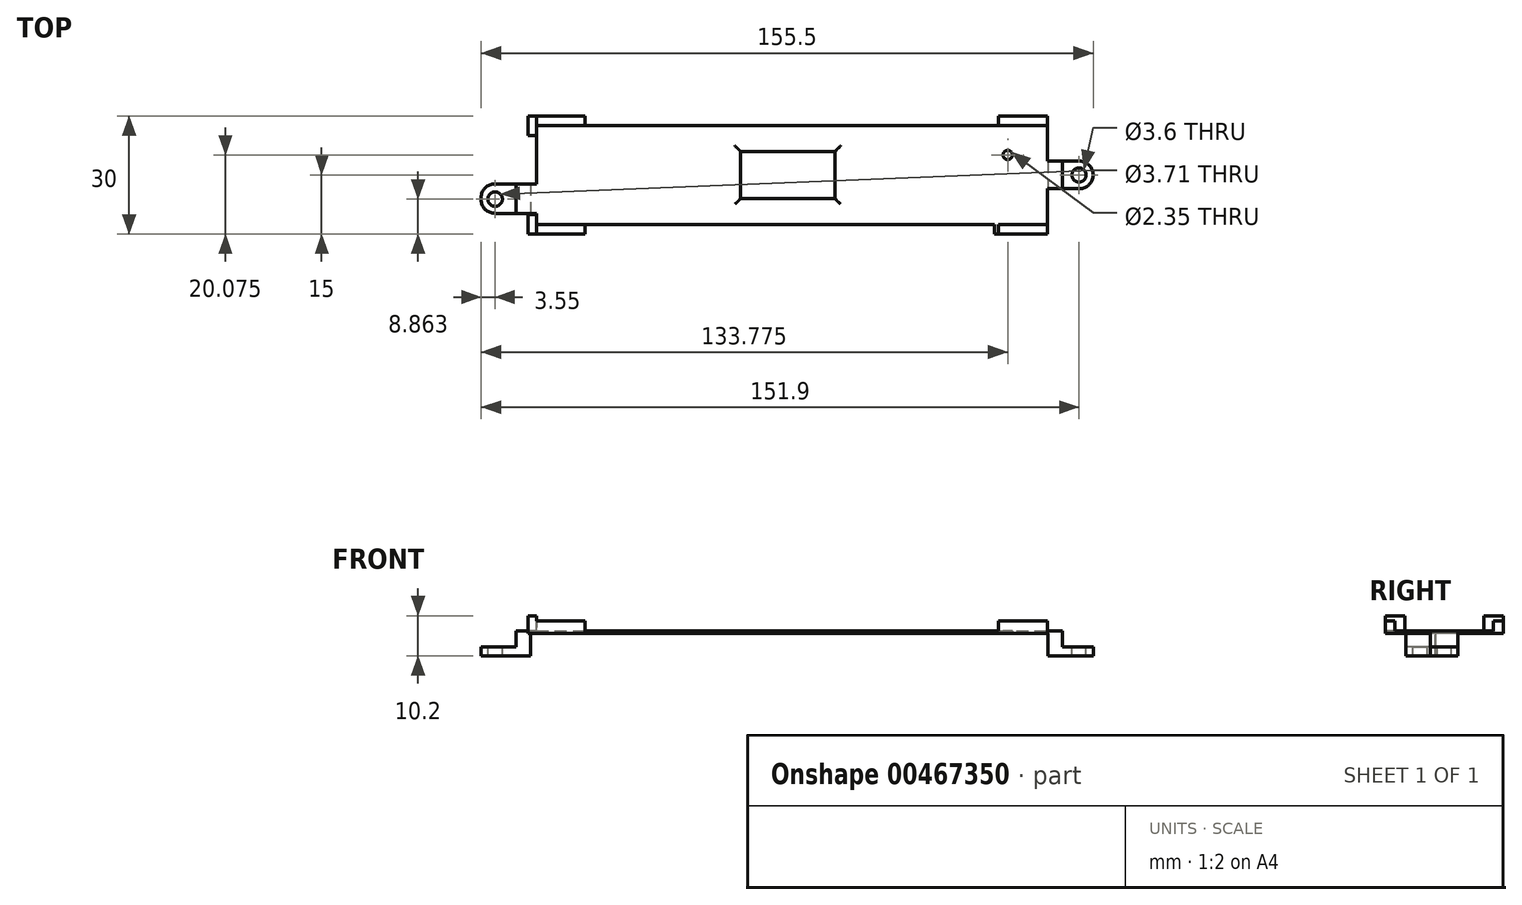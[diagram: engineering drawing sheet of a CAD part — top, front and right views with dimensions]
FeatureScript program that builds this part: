
annotation { "Feature Type Name" : "Feature", "Feature Type Description" : "" }
export const myFeature = defineFeature(function(context is Context, id is Id, definition is map)
    precondition{}
    {
        {
            var Q0;
            Q0=qCreatedBy(makeId("Top.planeOp"),FACE);
            var sketch = newSketch(context, id + "F0", { "sketchPlane" : qUnion([Q0])});
            skLineSegment(sketch, "E0.bottom", {"start": v(-66, 15) * mm, "end": v(-51.5, 15) * mm});
            skLineSegment(sketch, "E0.top", {"start": v(-66, -15) * mm, "end": v(-51.5, -15) * mm});
            skLineSegment(sketch, "E0.left", {"start": v(-66, 15) * mm, "end": v(-66, 10) * mm});
            skLineSegment(sketch, "E0.right", {"start": v(66, 15) * mm, "end": v(66, -15) * mm});
            skLineSegment(sketch, "E1.bottom", {"start": v(-51.5, 12.55) * mm, "end": v(53.5, 12.55) * mm});
            skLineSegment(sketch, "E1.top", {"start": v(-51.5, -12.55) * mm, "end": v(52.5, -12.55) * mm});
            skLineSegment(sketch, "E2", {"start": v(-51.5, 12.55) * mm, "end": v(-51.5, 15) * mm});
            skLineSegment(sketch, "E3", {"start": v(-51.5, -12.55) * mm, "end": v(-51.5, -15) * mm});
            skLineSegment(sketch, "E4", {"start": v(52.5, -12.55) * mm, "end": v(52.5, -15) * mm});
            skLineSegment(sketch, "E5", {"start": v(53.5, 12.55) * mm, "end": v(53.5, 15) * mm});
            skLineSegment(sketch, "E6.trimOffspring", {"start": v(52.5, -15) * mm, "end": v(66, -15) * mm});
            skLineSegment(sketch, "E7.trimOffspring", {"start": v(53.5, 15) * mm, "end": v(66, 15) * mm});
            skLineSegment(sketch, "E8.bottom", {"start": v(-12, 6) * mm, "end": v(12, 6) * mm});
            skLineSegment(sketch, "E8.top", {"start": v(-12, -6) * mm, "end": v(12, -6) * mm});
            skLineSegment(sketch, "E8.left", {"start": v(-12, 6) * mm, "end": v(-12, -6) * mm});
            skLineSegment(sketch, "E8.right", {"start": v(12, 6) * mm, "end": v(12, -6) * mm});
            skLineSegment(sketch, "E9.bottom", {"start": v(-66, 10) * mm, "end": v(-63.8, 10) * mm});
            skLineSegment(sketch, "E9.top", {"start": v(-66, -10) * mm, "end": v(-63.8, -10) * mm});
            skLineSegment(sketch, "E9.right", {"start": v(-63.8, 10) * mm, "end": v(-63.8, -10) * mm});
            skLineSegment(sketch, "E10.trimOffspring", {"start": v(-66, -10) * mm, "end": v(-66, -15) * mm});
            skSolve(sketch);
        }
        {
            var Q0;
            Q0 = qSketchRegion(id + "F0", true);
            extrude(context, id + "F1", {"entities" : qUnion([Q0]), "depth" : 4.5 * mm});
        }
        {
            var Q0;
            Q0=makeQuery(id+"F1.opExtrude","CAP_FACE",FACE,{"disambiguationData":[OSD([sQuery(id+"F0.wireOp",EDGE,"E0.bottom"),sQuery(id+"F0.wireOp",EDGE,"E0.top"),sQuery(id+"F0.wireOp",EDGE,"E0.left"),sQuery(id+"F0.wireOp",EDGE,"E0.right"),sQuery(id+"F0.wireOp",EDGE,"E1.bottom"),sQuery(id+"F0.wireOp",EDGE,"E1.top"),sQuery(id+"F0.wireOp",EDGE,"E2"),sQuery(id+"F0.wireOp",EDGE,"E3"),sQuery(id+"F0.wireOp",EDGE,"E4"),sQuery(id+"F0.wireOp",EDGE,"E5"),sQuery(id+"F0.wireOp",EDGE,"E6.trimOffspring"),sQuery(id+"F0.wireOp",EDGE,"E7.trimOffspring"),sQuery(id+"F0.wireOp",EDGE,"E8.bottom"),sQuery(id+"F0.wireOp",EDGE,"E8.top"),sQuery(id+"F0.wireOp",EDGE,"E8.left"),sQuery(id+"F0.wireOp",EDGE,"E8.right")])],"isStart":false});
            var sketch = newSketch(context, id + "F2", { "sketchPlane" : qUnion([Q0])});
            skLineSegment(sketch, "E11.bottom", {"start": v(-63.8, 17.54) * mm, "end": v(70.25, 17.54) * mm});
            skLineSegment(sketch, "E11.top", {"start": v(-63.8, -19.78) * mm, "end": v(70.25, -19.78) * mm});
            skLineSegment(sketch, "E11.left", {"start": v(-63.8, 17.54) * mm, "end": v(-63.8, -19.78) * mm});
            skLineSegment(sketch, "E11.right", {"start": v(70.25, 17.54) * mm, "end": v(70.25, -19.78) * mm});
            skSolve(sketch);
        }
        {
            var Q0;
            Q0 = qSketchRegion(id + "F2", true);
            extrude(context, id + "F3", {"entities" : qUnion([Q0]), "operationType" : NewBodyOperationType.REMOVE, "oppositeDirection" : true, "depth" : 1.3 * mm});
        }
        {
            var Q0;
            Q0=makeQuery(id+"F3.boolean.opBoolean","COPY",FACE,{"derivedFrom":makeQuery(id+"F3.opExtrude","CAP_FACE",FACE,{"disambiguationData":[OSD([sQuery(id+"F2.wireOp",EDGE,"E11.bottom"),sQuery(id+"F2.wireOp",EDGE,"E11.top"),sQuery(id+"F2.wireOp",EDGE,"E11.left"),sQuery(id+"F2.wireOp",EDGE,"E11.right")])],"isStart":false})});
            var sketch = newSketch(context, id + "F4", { "sketchPlane" : qUnion([Q0])});
            skLineSegment(sketch, "E12.top", {"start": v(-63.8, -12.55) * mm, "end": v(-51.5, -12.55) * mm});
            skLineSegment(sketch, "E12.left", {"start": v(-63.8, 12.5) * mm, "end": v(-63.8, -12.55) * mm});
            skLineSegment(sketch, "E12.right", {"start": v(68.76, 12.5) * mm, "end": v(68.76, -12.55) * mm});
            skLineSegment(sketch, "E13.top", {"start": v(-51.5, 21.08) * mm, "end": v(53.5, 21.08) * mm});
            skLineSegment(sketch, "E13.left", {"start": v(-51.5, 12.55) * mm, "end": v(-51.5, 21.08) * mm});
            skLineSegment(sketch, "E13.right", {"start": v(53.5, 12.55) * mm, "end": v(53.5, 21.08) * mm});
            skLineSegment(sketch, "E14.top", {"start": v(-51.5, -30.05) * mm, "end": v(53.5, -30.05) * mm});
            skLineSegment(sketch, "E14.left", {"start": v(-51.5, -12.55) * mm, "end": v(-51.5, -30.05) * mm});
            skLineSegment(sketch, "E14.right", {"start": v(53.5, -12.55) * mm, "end": v(53.5, -30.05) * mm});
            skLineSegment(sketch, "E15.trimOffspring", {"start": v(53.5, -12.55) * mm, "end": v(68.76, -12.55) * mm});
            skLineSegment(sketch, "E16", {"start": v(-51.5, 12.55) * mm, "end": v(-63.8, 12.5) * mm});
            skLineSegment(sketch, "E17", {"start": v(68.76, 12.5) * mm, "end": v(53.5, 12.55) * mm});
            skSolve(sketch);
        }
        {
            var Q0;
            Q0 = qSketchRegion(id + "F4", true);
            extrude(context, id + "F5", {"entities" : qUnion([Q0]), "operationType" : NewBodyOperationType.REMOVE, "oppositeDirection" : true, "depth" : 2.6 * mm});
        }
        {
            var Q0;
            Q0=makeQuery(id+"F5.boolean.opBoolean","COPY",FACE,{"derivedFrom":makeQuery(id+"F5.opExtrude","CAP_FACE",FACE,{"disambiguationData":[OSD([sQuery(id+"F4.wireOp",EDGE,"E12.bottom"),sQuery(id+"F4.wireOp",EDGE,"E12.top"),sQuery(id+"F4.wireOp",EDGE,"E12.left"),sQuery(id+"F4.wireOp",EDGE,"E12.right")])],"isStart":false})});
            var sketch = newSketch(context, id + "F6", { "sketchPlane" : qUnion([Q0])});
            skLineSegment(sketch, "E18.bottom", {"start": v(66, -3.5) * mm, "end": v(74.1, -3.5) * mm});
            skLineSegment(sketch, "E18.top", {"start": v(66, 3.5) * mm, "end": v(74.1, 3.5) * mm});
            skLineSegment(sketch, "E18.left", {"start": v(66, -3.5) * mm, "end": v(66, 3.5) * mm});
            skLineSegment(sketch, "E18.right", {"start": v(77.6, 0) * mm, "end": v(77.6, 0) * mm});
            skCircle(sketch, "E19", {"center": v(74, 0) * mm, "radius": 1.8 * mm});
            skPoint(sketch, "E20.visualSharp", {"position": v(77.6, -3.5) * mm});
            skArc(sketch, "E20.filletArc", {"start": v(74.1, -3.5) * mm, "mid": v(76.57, -2.47) * mm, "end": v(77.6, 0) * mm});
            skPoint(sketch, "E21.visualSharp", {"position": v(77.6, 3.5) * mm});
            skArc(sketch, "E21.filletArc", {"start": v(77.6, 0) * mm, "mid": v(76.57, 2.47) * mm, "end": v(74.1, 3.5) * mm});
            skLineSegment(sketch, "E22.bottom", {"start": v(-63.8, -9.75) * mm, "end": v(-74.4, -9.75) * mm});
            skLineSegment(sketch, "E22.top", {"start": v(-63.8, -2.25) * mm, "end": v(-74.4, -2.25) * mm});
            skLineSegment(sketch, "E22.left", {"start": v(-63.8, -9.75) * mm, "end": v(-63.8, -2.25) * mm});
            skLineSegment(sketch, "E22.right", {"start": v(-77.9, -6.25) * mm, "end": v(-77.9, -5.75) * mm});
            skCircle(sketch, "E23", {"center": v(-74.35, -6.14) * mm, "radius": 1.85 * mm});
            skPoint(sketch, "E24.visualSharp", {"position": v(-77.9, -9.75) * mm});
            skArc(sketch, "E24.filletArc", {"start": v(-77.9, -6.25) * mm, "mid": v(-76.87, -8.72) * mm, "end": v(-74.4, -9.75) * mm});
            skPoint(sketch, "E25.visualSharp", {"position": v(-77.9, -2.25) * mm});
            skArc(sketch, "E25.filletArc", {"start": v(-74.4, -2.25) * mm, "mid": v(-76.87, -3.28) * mm, "end": v(-77.9, -5.75) * mm});
            skSolve(sketch);
        }
        {
            var Q0;
            Q0 = qSketchRegion(id + "F6", true);
            extrude(context, id + "F7", {"entities" : qUnion([Q0]), "operationType" : NewBodyOperationType.ADD, "oppositeDirection" : true, "depth" : 6.3 * mm});
        }
        {
            var Q0;
            Q0=makeQuery(id+"F7.opExtrude","CAP_FACE",FACE,{"disambiguationData":[OSD([sQuery(id+"F6.wireOp",EDGE,"E22.bottom"),sQuery(id+"F6.wireOp",EDGE,"E22.top"),sQuery(id+"F6.wireOp",EDGE,"E22.left"),sQuery(id+"F6.wireOp",EDGE,"E23"),sQuery(id+"F6.wireOp",EDGE,"E24.filletArc"),sQuery(id+"F6.wireOp",EDGE,"E25.filletArc")])],"isStart":false});
            var sketch = newSketch(context, id + "F8", { "sketchPlane" : qUnion([Q0])});
            skLineSegment(sketch, "E26.bottom", {"start": v(66.1, -31.39) * mm, "end": v(-65.37, -31.39) * mm});
            skLineSegment(sketch, "E26.top", {"start": v(66.1, 26.27) * mm, "end": v(-65.37, 26.27) * mm});
            skLineSegment(sketch, "E26.left", {"start": v(66.1, -31.39) * mm, "end": v(66.1, 26.27) * mm});
            skLineSegment(sketch, "E26.right", {"start": v(-65.37, -31.39) * mm, "end": v(-65.37, 26.27) * mm});
            skSolve(sketch);
        }
        {
            var Q0;
            Q0 = qSketchRegion(id + "F8", true);
            var Q1;
            Q1=makeQuery(id+"F1.opExtrude","CAP_FACE",FACE,{"disambiguationData":[OSD([sQuery(id+"F0.wireOp",EDGE,"E0.bottom"),sQuery(id+"F0.wireOp",EDGE,"E0.top"),sQuery(id+"F0.wireOp",EDGE,"E0.left"),sQuery(id+"F0.wireOp",EDGE,"E0.right"),sQuery(id+"F0.wireOp",EDGE,"E1.bottom"),sQuery(id+"F0.wireOp",EDGE,"E1.top"),sQuery(id+"F0.wireOp",EDGE,"E2"),sQuery(id+"F0.wireOp",EDGE,"E3"),sQuery(id+"F0.wireOp",EDGE,"E4"),sQuery(id+"F0.wireOp",EDGE,"E5"),sQuery(id+"F0.wireOp",EDGE,"E6.trimOffspring"),sQuery(id+"F0.wireOp",EDGE,"E7.trimOffspring"),sQuery(id+"F0.wireOp",EDGE,"E8.bottom"),sQuery(id+"F0.wireOp",EDGE,"E8.top"),sQuery(id+"F0.wireOp",EDGE,"E8.left"),sQuery(id+"F0.wireOp",EDGE,"E8.right"),sQuery(id+"F0.wireOp",EDGE,"E9.bottom"),sQuery(id+"F0.wireOp",EDGE,"E9.top"),sQuery(id+"F0.wireOp",EDGE,"E9.right"),sQuery(id+"F0.wireOp",EDGE,"E10.trimOffspring")])],"isStart":true});
            extrude(context, id + "F9", {"entities" : qUnion([Q0]), "operationType" : NewBodyOperationType.REMOVE, "endBound" : BoundingType.UP_TO_SURFACE, "oppositeDirection" : true, "endBoundEntityFace" : qUnion([Q1]), "depth" : 25 * mm});
        }
        {
            var Q0;
            {var subQ0=sQuery(id+"F0.wireOp",EDGE,"E10.trimOffspring");var subQ1=sQuery(id+"F0.wireOp",EDGE,"E9.right");var subQ2=sQuery(id+"F0.wireOp",EDGE,"E9.top");var subQ3=sQuery(id+"F0.wireOp",EDGE,"E9.bottom");var subQ4=sQuery(id+"F0.wireOp",EDGE,"E8.right");var subQ5=sQuery(id+"F0.wireOp",EDGE,"E8.left");var subQ6=sQuery(id+"F0.wireOp",EDGE,"E8.top");var subQ7=sQuery(id+"F0.wireOp",EDGE,"E8.bottom");var subQ8=sQuery(id+"F0.wireOp",EDGE,"E7.trimOffspring");var subQ9=sQuery(id+"F0.wireOp",EDGE,"E6.trimOffspring");var subQ10=sQuery(id+"F0.wireOp",EDGE,"E5");var subQ11=sQuery(id+"F0.wireOp",EDGE,"E4");var subQ12=sQuery(id+"F0.wireOp",EDGE,"E3");var subQ13=sQuery(id+"F0.wireOp",EDGE,"E2");var subQ14=sQuery(id+"F0.wireOp",EDGE,"E1.top");var subQ15=sQuery(id+"F0.wireOp",EDGE,"E1.bottom");var subQ16=sQuery(id+"F0.wireOp",EDGE,"E0.right");var subQ17=sQuery(id+"F0.wireOp",EDGE,"E0.left");var subQ18=sQuery(id+"F0.wireOp",EDGE,"E0.top");var subQ19=sQuery(id+"F0.wireOp",EDGE,"E0.bottom");Q0=makeQuery(id+"F9.boolean.opBoolean","MERGE",FACE,{"derivedFrom":[makeQuery(id+"F1.opExtrude","CAP_FACE",FACE,{"disambiguationData":[OSD([subQ19,subQ18,subQ17,subQ16,subQ15,subQ14,subQ13,subQ12,subQ11,subQ10,subQ9,subQ8,subQ7,subQ6,subQ5,subQ4,subQ3,subQ2,subQ1,subQ0])],"isStart":true}),makeQuery(id+"F9.opExtrude","CAP_FACE",FACE,{"disambiguationData":[OSD([subQ19,subQ18,subQ17,subQ16,subQ15,subQ14,subQ13,subQ12,subQ11,subQ10,subQ9,subQ8,subQ7,subQ6,subQ5,subQ4,subQ3,subQ2,subQ1,subQ0])],"isStart":false})]});}
            var sketch = newSketch(context, id + "F10", { "sketchPlane" : qUnion([Q0])});
            skCircle(sketch, "E27", {"center": v(55.88, -5.07) * mm, "radius": 1.18 * mm});
            skSolve(sketch);
        }
        {
            var Q0;
            Q0 = qSketchRegion(id + "F10", true);
            extrude(context, id + "F11", {"entities" : qUnion([Q0]), "operationType" : NewBodyOperationType.REMOVE, "oppositeDirection" : true, "depth" : 2 * mm});
        }
        {
            var Q0;
            Q0=makeQuery(id+"F7.boolean.opBoolean","MERGE",FACE,{"derivedFrom":[makeQuery(id+"F5.boolean.opBoolean","COPY",FACE,{"derivedFrom":makeQuery(id+"F5.opExtrude","CAP_FACE",FACE,{"disambiguationData":[OSD([sQuery(id+"F4.wireOp",EDGE,"E12.bottom"),sQuery(id+"F4.wireOp",EDGE,"E12.top"),sQuery(id+"F4.wireOp",EDGE,"E12.left"),sQuery(id+"F4.wireOp",EDGE,"E12.right")])],"isStart":false})}),makeQuery(id+"F7.opExtrude","CAP_FACE",FACE,{"disambiguationData":[OSD([sQuery(id+"F6.wireOp",EDGE,"E18.bottom"),sQuery(id+"F6.wireOp",EDGE,"E18.top"),sQuery(id+"F6.wireOp",EDGE,"E18.left"),sQuery(id+"F6.wireOp",EDGE,"E19"),sQuery(id+"F6.wireOp",EDGE,"E20.filletArc"),sQuery(id+"F6.wireOp",EDGE,"E21.filletArc")])],"isStart":true}),makeQuery(id+"F7.opExtrude","CAP_FACE",FACE,{"disambiguationData":[OSD([sQuery(id+"F6.wireOp",EDGE,"E22.bottom"),sQuery(id+"F6.wireOp",EDGE,"E22.top"),sQuery(id+"F6.wireOp",EDGE,"E22.left"),sQuery(id+"F6.wireOp",EDGE,"E23"),sQuery(id+"F6.wireOp",EDGE,"E24.filletArc"),sQuery(id+"F6.wireOp",EDGE,"E25.filletArc")])],"isStart":true})]});
            var sketch = newSketch(context, id + "F12", { "sketchPlane" : qUnion([Q0])});
            skLineSegment(sketch, "E28.bottom", {"start": v(-83.88, 15.75) * mm, "end": v(-69.02, 15.75) * mm});
            skLineSegment(sketch, "E28.top", {"start": v(-83.88, -17.96) * mm, "end": v(-69.02, -17.96) * mm});
            skLineSegment(sketch, "E28.left", {"start": v(-83.88, 15.75) * mm, "end": v(-83.88, -17.96) * mm});
            skLineSegment(sketch, "E28.right", {"start": v(-69.02, 15.75) * mm, "end": v(-69.02, -17.96) * mm});
            skLineSegment(sketch, "E29.bottom", {"start": v(69.75, 10.9) * mm, "end": v(85.4, 10.9) * mm});
            skLineSegment(sketch, "E29.top", {"start": v(69.75, -13.4) * mm, "end": v(85.4, -13.4) * mm});
            skLineSegment(sketch, "E29.left", {"start": v(69.75, 10.9) * mm, "end": v(69.75, -13.4) * mm});
            skLineSegment(sketch, "E29.right", {"start": v(85.4, 10.9) * mm, "end": v(85.4, -13.4) * mm});
            skSolve(sketch);
        }
        {
            var Q0;
            Q0=makeQuery(id+"F12.imprint","IMPRINT",FACE,{"disambiguationData":[TD([[makeQuery(id+"F12.imprint","IMPRINT",EDGE,{"derivedFrom":makeQuery(id+"F7.opExtrude","CAP_EDGE",EDGE,{"disambiguationData":[OSD([sQuery(id+"F6.wireOp",EDGE,"E23")])],"isStart":true})}),-1.0]])]});
            var Q1;
            Q1=makeQuery(id+"F12.imprint","IMPRINT",FACE,{"disambiguationData":[TD([[makeQuery(id+"F12.imprint","IMPRINT",EDGE,{"derivedFrom":makeQuery(id+"F7.opExtrude","CAP_EDGE",EDGE,{"disambiguationData":[OSD([sQuery(id+"F6.wireOp",EDGE,"E19")])],"isStart":true})}),-1.0]])]});
            extrude(context, id + "F13", {"entities" : qUnion([Q0, Q1]), "operationType" : NewBodyOperationType.REMOVE, "oppositeDirection" : true, "depth" : 4 * mm});
        }
        {
            var Q0;
            Q0=makeQuery(id+"F5.boolean.opBoolean","INTERSECT",EDGE,{"derivedFrom":[makeQuery(id+"F1.opExtrude","SWEPT_FACE",FACE,{"disambiguationData":[OSD([sQuery(id+"F0.wireOp",EDGE,"E8.bottom")])]}),makeQuery(id+"F5.opExtrude","CAP_FACE",FACE,{"disambiguationData":[OSD([sQuery(id+"F4.wireOp",EDGE,"E12.bottom"),sQuery(id+"F4.wireOp",EDGE,"E12.top"),sQuery(id+"F4.wireOp",EDGE,"E12.left"),sQuery(id+"F4.wireOp",EDGE,"E12.right")])],"isStart":false})]});
            var Q1;
            Q1=makeQuery(id+"F5.boolean.opBoolean","INTERSECT",EDGE,{"derivedFrom":[makeQuery(id+"F1.opExtrude","SWEPT_FACE",FACE,{"disambiguationData":[OSD([sQuery(id+"F0.wireOp",EDGE,"E8.left")])]}),makeQuery(id+"F5.opExtrude","CAP_FACE",FACE,{"disambiguationData":[OSD([sQuery(id+"F4.wireOp",EDGE,"E12.bottom"),sQuery(id+"F4.wireOp",EDGE,"E12.top"),sQuery(id+"F4.wireOp",EDGE,"E12.left"),sQuery(id+"F4.wireOp",EDGE,"E12.right")])],"isStart":false})]});
            var Q2;
            Q2=makeQuery(id+"F5.boolean.opBoolean","INTERSECT",EDGE,{"derivedFrom":[makeQuery(id+"F1.opExtrude","SWEPT_FACE",FACE,{"disambiguationData":[OSD([sQuery(id+"F0.wireOp",EDGE,"E8.top")])]}),makeQuery(id+"F5.opExtrude","CAP_FACE",FACE,{"disambiguationData":[OSD([sQuery(id+"F4.wireOp",EDGE,"E12.bottom"),sQuery(id+"F4.wireOp",EDGE,"E12.top"),sQuery(id+"F4.wireOp",EDGE,"E12.left"),sQuery(id+"F4.wireOp",EDGE,"E12.right")])],"isStart":false})]});
            var Q3;
            Q3=makeQuery(id+"F5.boolean.opBoolean","INTERSECT",EDGE,{"derivedFrom":[makeQuery(id+"F1.opExtrude","SWEPT_FACE",FACE,{"disambiguationData":[OSD([sQuery(id+"F0.wireOp",EDGE,"E8.right")])]}),makeQuery(id+"F5.opExtrude","CAP_FACE",FACE,{"disambiguationData":[OSD([sQuery(id+"F4.wireOp",EDGE,"E12.bottom"),sQuery(id+"F4.wireOp",EDGE,"E12.top"),sQuery(id+"F4.wireOp",EDGE,"E12.left"),sQuery(id+"F4.wireOp",EDGE,"E12.right")])],"isStart":false})]});
            fillet(context, id + "F14", {"entities" : qUnion([Q0, Q1, Q2, Q3]), "radius" : 2 * mm, "tangentPropagation" : true, "allowEdgeOverflow" : false});
        }
    });
